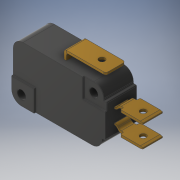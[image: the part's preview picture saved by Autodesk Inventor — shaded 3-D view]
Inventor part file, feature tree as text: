
AUTODESK INVENTOR PART (.ipt)
format: ipt  version: 2017.1 (Build 211199000, 199)  size: 411,648 bytes
history: native  units: in
note: dims shown in document units (in); Inventor stores cm internally (conversion verified against a paired STEP export)
features: sketch x11, fillet x9, extrude x8, plane x5, hole x3, other x2, mirror x1, projected_geometry x1
ambient origin geometry x8: Origin, YZ Plane, XZ Plane, XY Plane, X Axis, Y Axis, Z Axis, Center Point
bodies: Solid1 (feature_tree)
feature tree (40):
  sketch  "Sketch1"  dims[d15=1.17in d18=0.4in d19=0.0in d20=0.125in]
  extrude  "Extrusion1"  Depth=0.4in TaperAngle=0.0deg
  fillet  "Fillet1"  Radius=0.125in
  extrude  "Extrusion2"  Depth=0.01in
  fillet  "Fillet2"  Radius=0.02in
  hole  "Hole1"  [1 undecoded]
  sketch  "Sketch3"  dims[d24=0.11in d25=0.75in d26=0.375in d27=0.25in d28=0.5635in d29=1.0in d30=0.8108in d33=0.02in d34=0.0in]
  extrude  "Extrusion4"  Depth=0.005in
  fillet  "Fillet3"  Radius=0.57in
  extrude  "Extrusion5"  Depth=0.015in
  fillet  "Fillet4"  Radius=0.0075in
  plane  "Work Plane2"
  plane  "Work Plane3"
  extrude  "Extrusion6"  Depth=0.05in
  fillet  "Fillet5"  Radius=0.125in
  extrude  "Extrusion7"  TaperAngle=0.0deg  [1 undecoded]
  fillet  "Fillet6"  Radius=0.4in
  hole  "Hole2"  [1 undecoded]
  mirror  "Mirror1"
  plane  "Work Plane5"
  extrude  "Extrusion8"  Depth=0.03in TaperAngle=0.0deg
  extrude  "Extrusion9"  Depth=0.03in
  fillet  "Fillet7"  Radius=0.03in
  fillet  "Fillet8"  Radius=0.03in
  hole  "Hole3"  [1 undecoded]
  fillet  "Fillet9"  [1 undecoded]
  other  "Image1"
  sketch  "Sketch2"  dims[d21=0.2875in d22=0.0in d23=0.01in]
  sketch  "Sketch4"  dims[d35=0.005in d38=0.02in d39=0.0in]
  sketch  "Sketch6"  dims[d40=0.005in d41=0.151in d43=0.57in]
  plane  "Work Plane1"
  sketch  "Sketch9"  dims[d44=0.03in d47=0.015in d48=0.0075in]
  sketch  "Sketch10"  dims[d49=0.25in d50=0.0in d51=0.05in d52=0.125in d53=0.0in]
  sketch  "Sketch11"  dims[d54=0.01in]
  other  "Work Axis1"
  plane  "Work Plane4"
  sketch  "Sketch12"  dims[d55=0.075in d56=0.75in d57=0.375in d58=0.25in d59=0.5635in d60=1.0in d61=0.8108in d62=0.0in d63=-0.65in d64=0.4in]
  projected_geometry  "Projected Loop3"
  sketch  "Sketch13"  dims[d65=0.25in d66=0.075in]
  sketch  "Sketch14"  dims[d67=0.03in d68=0.0in d69=0.03in d70=0.0in d71=0.03in d72=0.03in d73=0.075in d74=0.75in d75=0.375in d76=0.25in d77=0.5635in d78=1.0in d79=0.8108in d80=0.03in]
note: 5 required parameter values undecoded (feature->parameter linkage not recoverable at this tier; creation-order binding heuristic only, values carry confidence <= 0.55)
